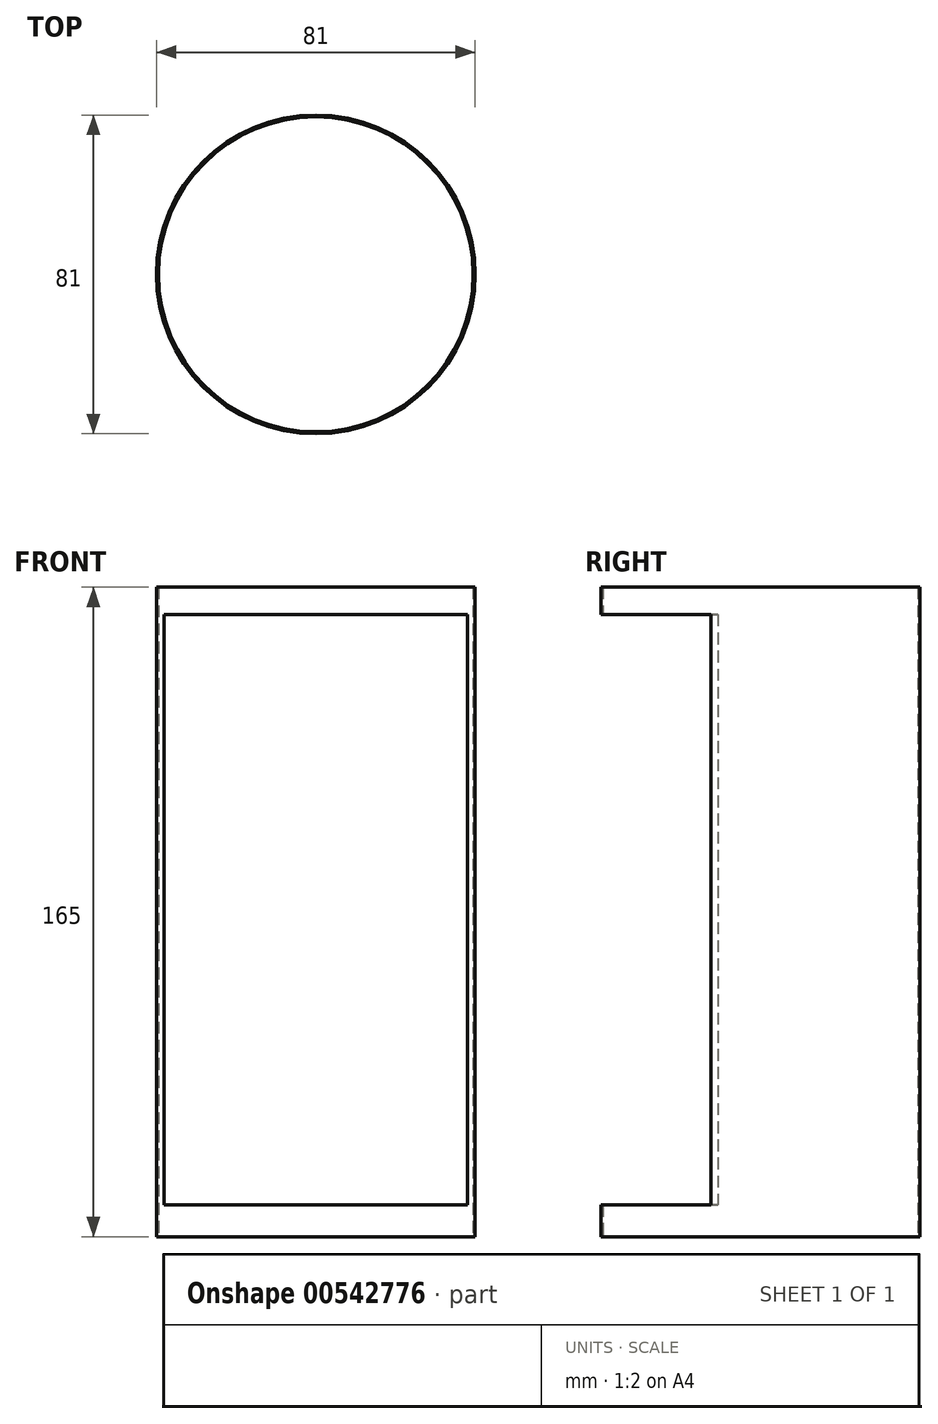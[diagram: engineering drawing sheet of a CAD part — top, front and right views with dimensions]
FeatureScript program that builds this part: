
annotation { "Feature Type Name" : "Feature", "Feature Type Description" : "" }
export const myFeature = defineFeature(function(context is Context, id is Id, definition is map)
    precondition{}
    {
        {
            var Q0;
            Q0=qCreatedBy(makeId("Top.planeOp"),FACE);
            var sketch = newSketch(context, id + "F0", { "sketchPlane" : qUnion([Q0])});
            skCircle(sketch, "E0", {"center": v(0, 0) * mm, "radius": 40.5 * mm});
            skSolve(sketch);
        }
        {
            var Q0;
            Q0=makeQuery(id+"F0.imprint","IMPRINT",FACE,{"disambiguationData":[TD([[makeQuery(id+"F0.imprint","IMPRINT",EDGE,{"derivedFrom":sQuery(id+"F0.wireOp",EDGE,"E0")}),1.0]])]});
            var Q1;
            Q1=sQuery(id+"F0.wireOp",EDGE,"E0");
            extrude(context, id + "F1", {"entities" : qUnion([Q0]), "surfaceEntities" : qUnion([Q1]), "depth" : 165 * mm, "offsetDistance" : 25 * mm});
        }
        {
            var Q0;
            Q0=qCreatedBy(makeId("Front.planeOp"),FACE);
            var sketch = newSketch(context, id + "F2", { "sketchPlane" : qUnion([Q0])});
            skLineSegment(sketch, "E1.bottom", {"start": v(38.5, 8.08) * mm, "end": v(-38.5, 8.08) * mm});
            skLineSegment(sketch, "E1.top", {"start": v(38.5, 158.08) * mm, "end": v(-38.5, 158.08) * mm});
            skLineSegment(sketch, "E1.left", {"start": v(38.5, 8.08) * mm, "end": v(38.5, 158.08) * mm});
            skLineSegment(sketch, "E1.right", {"start": v(-38.5, 8.08) * mm, "end": v(-38.5, 158.08) * mm});
            skPoint(sketch, "E1.middle", {"position": v(0, 83.08) * mm});
            skSolve(sketch);
        }
        {
            var Q0;
            Q0 = qSketchRegion(id + "F2", true);
            extrude(context, id + "F3", {"entities" : qUnion([Q0]), "operationType" : NewBodyOperationType.REMOVE, "depth" : 50 * mm, "offsetDistance" : 25 * mm});
        }
        {
            var Q0;
            Q0=makeQuery(id+"F1.opExtrude","CAP_FACE",FACE,{"disambiguationData":[OSD([sQuery(id+"F0.wireOp",EDGE,"E0")])],"isStart":false});
            shell(context, id + "F4", {"entities" : qUnion([Q0]), "thickness" : 1.5 * mm});
        }
        {
            var Q0;
            Q0=qCreatedBy(makeId("Top.planeOp"),FACE);
            var sketch = newSketch(context, id + "F5", { "sketchPlane" : qUnion([Q0])});
            skCircle(sketch, "E2", {"center": v(0, 0) * mm, "radius": 40 * mm});
            skSolve(sketch);
        }
        {
            var Q0;
            Q0 = qSketchRegion(id + "F5", true);
            extrude(context, id + "F6", {"entities" : qUnion([Q0]), "operationType" : NewBodyOperationType.REMOVE, "depth" : 165 * mm, "offsetDistance" : 25 * mm});
        }
    });
